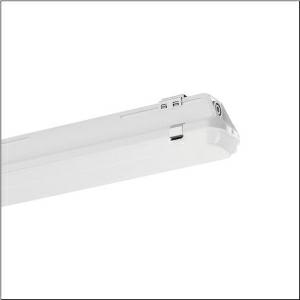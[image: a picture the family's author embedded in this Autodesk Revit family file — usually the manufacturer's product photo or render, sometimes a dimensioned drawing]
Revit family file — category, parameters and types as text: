
# Revit family: monsun_11_emergency_51fp107p467l3g
name_source: partatom
category: Lighting Fixtures
units: mm (PartAtom-declared; Revit-internal decimal feet)

## family parameters
Cut with Voids When Loaded = No
Host = Face
Light Source = No
Part Type = Normal
Room Calculation Point = No
Round Connector Dimension = Use Diameter
Shared = No

## types (1)
- --- (1 x LED, 990 lm, 6.5 W, 4000K)
    Apparent Load = 7 VA
    CIE Flux Codes = 47 77 93 94 100
    Color Rendering = 80
    Color Temperature = 4000K
    Default Elevation = 1800 mm
    Description = Monsun 11 emergency, damp-proof luminaire, chain hanger, primary optical cover: enclosure, of PMMA, light emission: direct distribution, primary light characteristic: symmetric, installation type: suspended mounting, surface-mounted, horizontal mounting, vertical mounting, LED, rated luminous flux: 6.050lm, luminous efficacy: 179lm/W, light colour: 840, colour temperature: 4000K, control gear: ON/OFF, with terminal, 4-pole, max. 2.5mm², mains connection: 220..240V, AC, 50/60Hz, rated input power: 37W, control gear: single battery element, battery: LiFePO4, 9Ah, luminaire housing, of glass-fibre reinforced polyester, uncoated, bright grey, incl. chain hanger, length: 1.590mm, width: 90mm, height: 88mm, clip for enclosure, of stainless steel (V2A), ceiling mounting element, of stainless steel (V2A), chain hanger, of stainless steel (V2A), protection rating (complete): IP66, insulation class (complete): insulation class I (protective earthing), certification: CE, UKCA, protection symbol: D, impact resistance: IK04, permissible operating ambient temperature: +5..+35°C, standard: EN 50419, EN 60598-2-1, EN 60598-2-22, contact your sales advisor before using the luminaires in applications with unclear chemical exposure, large temperature fluctuations or condensation-forming humidity, LABS conformity tested according to VDMA 24364:2018-05, no direct snow, no direct sun, no direct rain, for indoor or canopied outdoor use, corresponds to IFS (International Featured Standards) requirements for safety and quality in the food industry, packaging unit: 1 piece
    Height = 89 mm
    Lamp = 1 x LED
    Lamp Light Flux = 990 lm
    Lamp Power = 6.5 W
    Lamp count = 1
    Length = 1590 mm
    Luminous efficacy = 152 lm/W
    Manufacturer = Siteco
    ModVariant = No
    Model = 51FP107P467L3G
    Mounting Place = Ceiling
    Mounting Type = Surface mounted
    Number of Poles = 1
    OnlyDefault = Yes
    Power Factor = 1
    Product Name = Monsun 11 emergency
    Product group = damp-proof luminaire
    ProductGroupID = 300
    Protection Class = Protection class I
    Protection Degree = IP 66
    RLX_Detail_Level = 1
    RLX_Emergency_Light_Flux = 0 lm
    RLX_Emergency_Type = 0
    RLX_Emergency_Type_DB = No
    RlxData = <blob elided: 88777 chars, md5=39a48b17>
    Socket = socket
    Standby Power = 0 W
    System Light Flux = 990 lm
    System Power = 7 W
    Type Comments = : emergency light operation: 3 h
    Type Image = l_1349237.jpg
    URL = http://relux.com
    VarID = @adj_034067
    Voltage = 0 V
    Weight = 0.00 kg
    Width = 90 mm

## geometry (parser evidence)
native form markers: Blend x4, Sweep x15
no freeform markers — native parametric forms only
